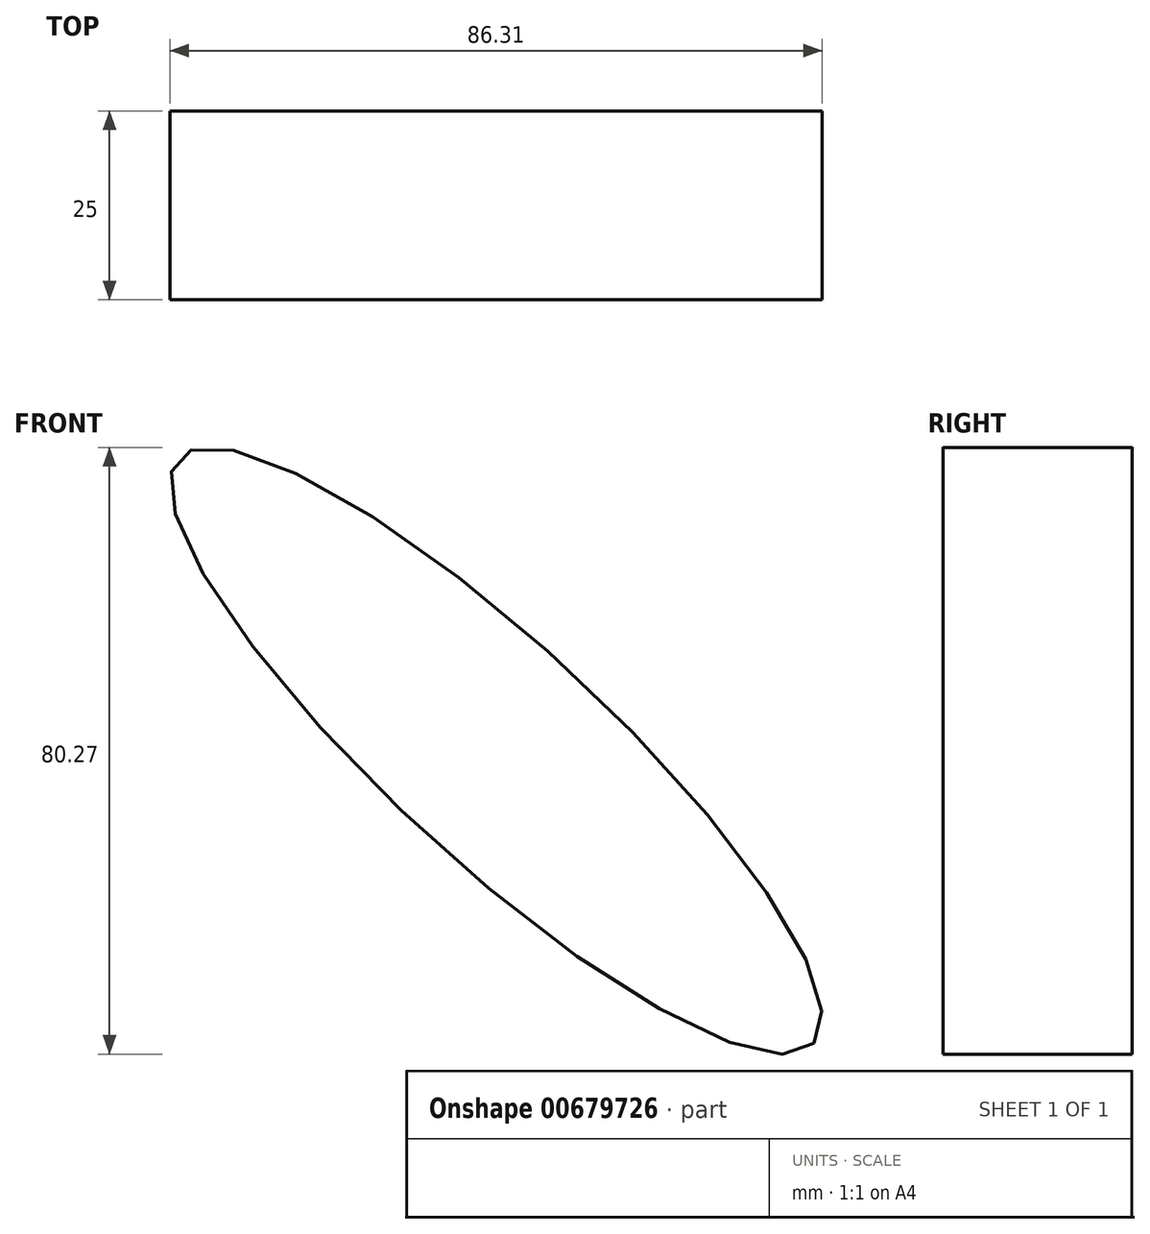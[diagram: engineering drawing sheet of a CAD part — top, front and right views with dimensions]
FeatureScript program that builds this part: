
annotation { "Feature Type Name" : "Feature", "Feature Type Description" : "" }
export const myFeature = defineFeature(function(context is Context, id is Id, definition is map)
    precondition{}
    {
        {
            var Q0;
            Q0=qCreatedBy(makeId("Front.planeOp"),FACE);
            var sketch = newSketch(context, id + "F0", { "sketchPlane" : qUnion([Q0])});
            skEllipse(sketch, "E0", {"center": v(-19.83, 23.51) * mm, "majorRadius": 57.17 * mm, "minorRadius": 14.33 * mm, "majorAxis": v(0.74, -0.68)});
            skSolve(sketch);
        }
        {
            var Q0;
            Q0=makeQuery(id+"F0.imprint","IMPRINT",FACE,{"disambiguationData":[TD([[makeQuery(id+"F0.imprint","IMPRINT",EDGE,{"derivedFrom":sQuery(id+"F0.wireOp",EDGE,"E0")}),1.0]])]});
            extrude(context, id + "F1", {"entities" : qUnion([Q0]), "endBound" : BoundingType.SYMMETRIC, "depth" : 25 * mm, "offsetDistance" : 25 * mm});
        }
    });
